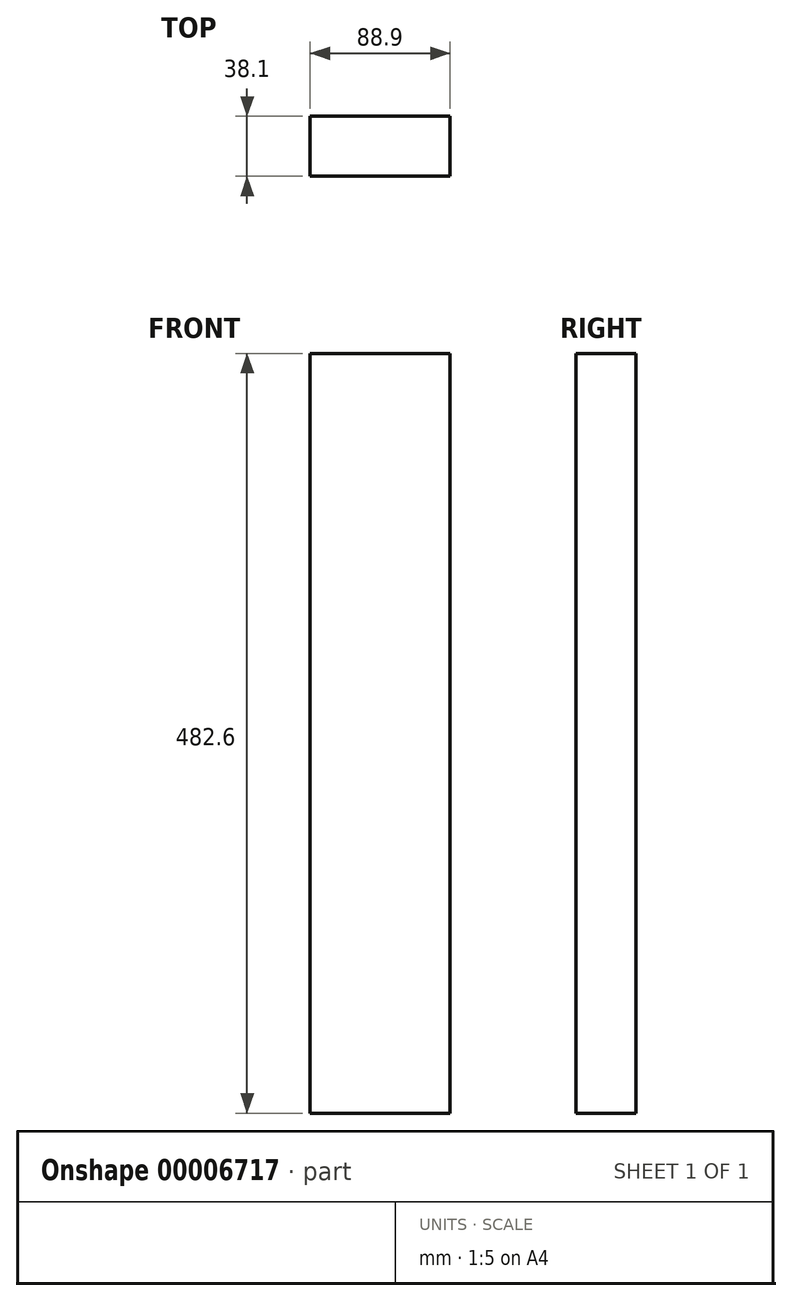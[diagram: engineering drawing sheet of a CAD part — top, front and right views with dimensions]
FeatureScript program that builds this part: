
annotation { "Feature Type Name" : "Feature", "Feature Type Description" : "" }
export const myFeature = defineFeature(function(context is Context, id is Id, definition is map)
    precondition{}
    {
        {
            var Q0;
            Q0=qCreatedBy(makeId("Top.planeOp"),FACE);
            var sketch = newSketch(context, id + "F0", { "sketchPlane" : qUnion([Q0])});
            skLineSegment(sketch, "E0.bottom", {"start": v(-69.85, 19.05) * mm, "end": v(19.05, 19.05) * mm});
            skLineSegment(sketch, "E0.top", {"start": v(-69.85, -19.05) * mm, "end": v(19.05, -19.05) * mm});
            skLineSegment(sketch, "E0.left", {"start": v(-69.85, 19.05) * mm, "end": v(-69.85, -19.05) * mm});
            skLineSegment(sketch, "E0.right", {"start": v(19.05, 19.05) * mm, "end": v(19.05, -19.05) * mm});
            skSolve(sketch);
        }
        {
            var Q0;
            Q0=qSketchRegion(id+"F0",true);
            extrude(context, id + "F1", {"entities" : qUnion([Q0]), "depth" : 482.6 * mm});
        }
    });
